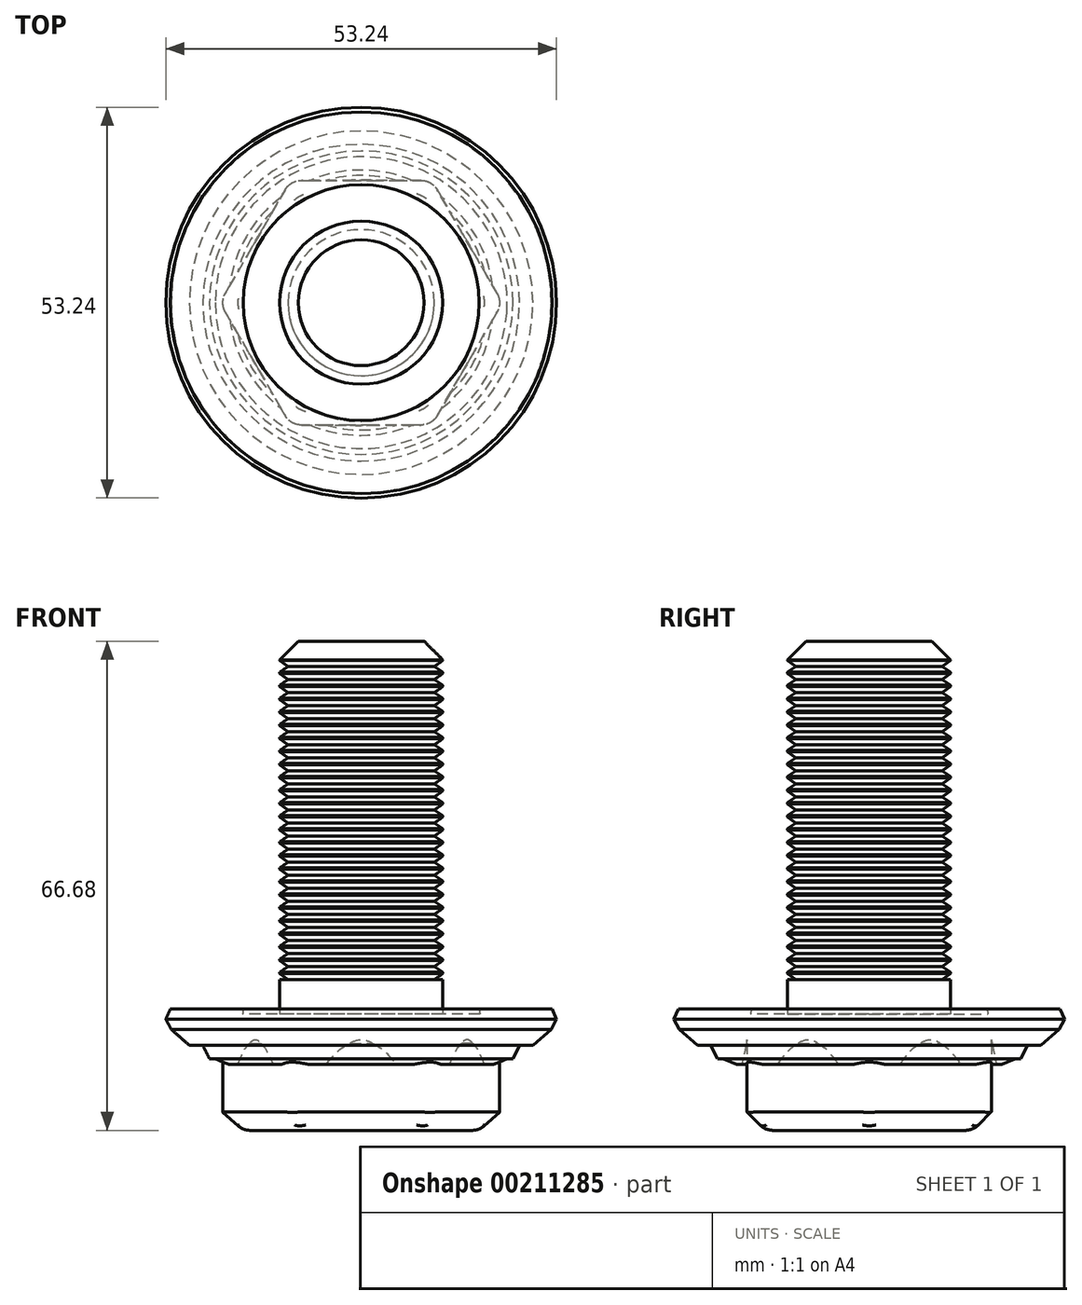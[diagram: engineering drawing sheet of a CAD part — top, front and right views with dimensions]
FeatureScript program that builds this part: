
annotation { "Feature Type Name" : "Feature", "Feature Type Description" : "" }
export const myFeature = defineFeature(function(context is Context, id is Id, definition is map)
    precondition{}
    {
        {
            var Q0;
            Q0=qCreatedBy(makeId("Top.planeOp"),FACE);
            var sketch = newSketch(context, id + "F0", { "sketchPlane" : qUnion([Q0])});
            skCircle(sketch, "E0.cCircle", {"center": v(0, 0) * mm, "radius": 16.67 * mm, "construction": true});
            skLineSegment(sketch, "E0.0", {"start": v(-9.62, 16.67) * mm, "end": v(9.62, 16.67) * mm});
            skLineSegment(sketch, "E0.1", {"start": v(9.62, 16.67) * mm, "end": v(19.25, 0) * mm});
            skLineSegment(sketch, "E0.2", {"start": v(19.25, 0) * mm, "end": v(9.62, -16.67) * mm});
            skLineSegment(sketch, "E0.3", {"start": v(9.62, -16.67) * mm, "end": v(-9.62, -16.67) * mm});
            skLineSegment(sketch, "E0.4", {"start": v(-9.62, -16.67) * mm, "end": v(-19.25, 0) * mm});
            skLineSegment(sketch, "E0.5", {"start": v(-19.25, 0) * mm, "end": v(-9.62, 16.67) * mm});
            skPoint(sketch, "E0.0.midPoint", {"position": v(0, 16.67) * mm});
            skSolve(sketch);
        }
        {
            var Q0;
            Q0=qSketchRegion(id+"F0",true);
            extrude(context, id + "F1", {"entities" : qUnion([Q0]), "depth" : 15.88 * mm});
        }
        {
            var Q0;
            Q0=makeQuery(id+"F1.opExtrude","CAP_FACE",FACE,{"disambiguationData":[OSD([sQuery(id+"F0.wireOp",EDGE,"E0.0"),sQuery(id+"F0.wireOp",EDGE,"E0.1"),sQuery(id+"F0.wireOp",EDGE,"E0.2"),sQuery(id+"F0.wireOp",EDGE,"E0.3"),sQuery(id+"F0.wireOp",EDGE,"E0.4"),sQuery(id+"F0.wireOp",EDGE,"E0.5")])],"isStart":false});
            var sketch = newSketch(context, id + "F2", { "sketchPlane" : qUnion([Q0])});
            skCircle(sketch, "E1", {"center": v(0, 0) * mm, "radius": 11.11 * mm});
            skSolve(sketch);
        }
        {
            var Q0;
            Q0=qSketchRegion(id+"F2",true);
            extrude(context, id + "F3", {"entities" : qUnion([Q0]), "operationType" : NewBodyOperationType.ADD, "depth" : 50.8 * mm});
        }
        {
            var Q0;
            Q0=makeQuery(id+"F3.opExtrude","CAP_EDGE",EDGE,{"disambiguationData":[OSD([sQuery(id+"F2.wireOp",EDGE,"E1")])],"isStart":false});
            var Q1;
            Q1=makeQuery(id+"F1.opExtrude","CAP_EDGE",EDGE,{"disambiguationData":[OSD([sQuery(id+"F0.wireOp",EDGE,"E0.5")])],"isStart":true});
            var Q2;
            Q2=makeQuery(id+"F1.opExtrude","CAP_EDGE",EDGE,{"disambiguationData":[OSD([sQuery(id+"F0.wireOp",EDGE,"E0.0")])],"isStart":true});
            var Q3;
            Q3=makeQuery(id+"F1.opExtrude","CAP_EDGE",EDGE,{"disambiguationData":[OSD([sQuery(id+"F0.wireOp",EDGE,"E0.1")])],"isStart":true});
            var Q4;
            Q4=makeQuery(id+"F1.opExtrude","CAP_EDGE",EDGE,{"disambiguationData":[OSD([sQuery(id+"F0.wireOp",EDGE,"E0.2")])],"isStart":true});
            var Q5;
            Q5=makeQuery(id+"F1.opExtrude","CAP_EDGE",EDGE,{"disambiguationData":[OSD([sQuery(id+"F0.wireOp",EDGE,"E0.3")])],"isStart":true});
            var Q6;
            Q6=makeQuery(id+"F1.opExtrude","CAP_EDGE",EDGE,{"disambiguationData":[OSD([sQuery(id+"F0.wireOp",EDGE,"E0.4")])],"isStart":true});
            chamfer(context, id + "F4", {"entities" : qUnion([Q0, Q1, Q2, Q3, Q4, Q5, Q6]), "width" : 2.54 * mm, "tangentPropagation" : true});
        }
        {
            var Q0;
            Q0=makeQuery(id+"F1.opExtrude","SWEPT_EDGE",EDGE,{"disambiguationData":[OSD([sQuery(id+"F0.wireOp",EDGE,"E0.0"),sQuery(id+"F0.wireOp",EDGE,"E0.5")])]});
            var Q1;
            Q1=makeQuery(id+"F1.opExtrude","SWEPT_EDGE",EDGE,{"disambiguationData":[OSD([sQuery(id+"F0.wireOp",EDGE,"E0.0"),sQuery(id+"F0.wireOp",EDGE,"E0.1")])]});
            var Q2;
            Q2=makeQuery(id+"F1.opExtrude","SWEPT_EDGE",EDGE,{"disambiguationData":[OSD([sQuery(id+"F0.wireOp",EDGE,"E0.1"),sQuery(id+"F0.wireOp",EDGE,"E0.2")])]});
            var Q3;
            Q3=makeQuery(id+"F1.opExtrude","SWEPT_EDGE",EDGE,{"disambiguationData":[OSD([sQuery(id+"F0.wireOp",EDGE,"E0.2"),sQuery(id+"F0.wireOp",EDGE,"E0.3")])]});
            var Q4;
            Q4=makeQuery(id+"F1.opExtrude","SWEPT_EDGE",EDGE,{"disambiguationData":[OSD([sQuery(id+"F0.wireOp",EDGE,"E0.3"),sQuery(id+"F0.wireOp",EDGE,"E0.4")])]});
            var Q5;
            Q5=makeQuery(id+"F1.opExtrude","SWEPT_EDGE",EDGE,{"disambiguationData":[OSD([sQuery(id+"F0.wireOp",EDGE,"E0.4"),sQuery(id+"F0.wireOp",EDGE,"E0.5")])]});
            var Q6;
            Q6=makeQuery(id+"F4.opChamfer","BLEND_EDGE",EDGE,{"blendedFrom":[makeQuery(id+"F1.opExtrude","CAP_EDGE",EDGE,{"disambiguationData":[OSD([sQuery(id+"F0.wireOp",EDGE,"E0.3")])],"isStart":true}),makeQuery(id+"F1.opExtrude","CAP_EDGE",EDGE,{"disambiguationData":[OSD([sQuery(id+"F0.wireOp",EDGE,"E0.4")])],"isStart":true})],"blendedInto":[]});
            var Q7;
            Q7=makeQuery(id+"F4.opChamfer","BLEND_EDGE",EDGE,{"blendedFrom":[makeQuery(id+"F1.opExtrude","CAP_EDGE",EDGE,{"disambiguationData":[OSD([sQuery(id+"F0.wireOp",EDGE,"E0.2")])],"isStart":true}),makeQuery(id+"F1.opExtrude","CAP_EDGE",EDGE,{"disambiguationData":[OSD([sQuery(id+"F0.wireOp",EDGE,"E0.3")])],"isStart":true})],"blendedInto":[]});
            var Q8;
            Q8=makeQuery(id+"F4.opChamfer","BLEND_EDGE",EDGE,{"blendedFrom":[makeQuery(id+"F1.opExtrude","CAP_EDGE",EDGE,{"disambiguationData":[OSD([sQuery(id+"F0.wireOp",EDGE,"E0.1")])],"isStart":true}),makeQuery(id+"F1.opExtrude","CAP_EDGE",EDGE,{"disambiguationData":[OSD([sQuery(id+"F0.wireOp",EDGE,"E0.2")])],"isStart":true})],"blendedInto":[]});
            var Q9;
            Q9=makeQuery(id+"F4.opChamfer","BLEND_EDGE",EDGE,{"blendedFrom":[makeQuery(id+"F1.opExtrude","CAP_EDGE",EDGE,{"disambiguationData":[OSD([sQuery(id+"F0.wireOp",EDGE,"E0.0")])],"isStart":true}),makeQuery(id+"F1.opExtrude","CAP_EDGE",EDGE,{"disambiguationData":[OSD([sQuery(id+"F0.wireOp",EDGE,"E0.1")])],"isStart":true})],"blendedInto":[]});
            var Q10;
            Q10=makeQuery(id+"F4.opChamfer","BLEND_EDGE",EDGE,{"blendedFrom":[makeQuery(id+"F1.opExtrude","CAP_EDGE",EDGE,{"disambiguationData":[OSD([sQuery(id+"F0.wireOp",EDGE,"E0.0")])],"isStart":true}),makeQuery(id+"F1.opExtrude","CAP_EDGE",EDGE,{"disambiguationData":[OSD([sQuery(id+"F0.wireOp",EDGE,"E0.5")])],"isStart":true})],"blendedInto":[]});
            var Q11;
            Q11=makeQuery(id+"F4.opChamfer","BLEND_EDGE",EDGE,{"blendedFrom":[makeQuery(id+"F1.opExtrude","CAP_EDGE",EDGE,{"disambiguationData":[OSD([sQuery(id+"F0.wireOp",EDGE,"E0.4")])],"isStart":true}),makeQuery(id+"F1.opExtrude","CAP_EDGE",EDGE,{"disambiguationData":[OSD([sQuery(id+"F0.wireOp",EDGE,"E0.5")])],"isStart":true})],"blendedInto":[]});
            var Q12;
            {var subQ0=sQuery(id+"F0.wireOp",EDGE,"E0.4");Q12=makeQuery(id+"F4.opChamfer","BLEND_EDGE",EDGE,{"blendedFrom":[makeQuery(id+"F1.opExtrude","CAP_EDGE",EDGE,{"disambiguationData":[OSD([subQ0])],"isStart":true}),makeQuery(id+"F1.opExtrude","CAP_FACE",FACE,{"disambiguationData":[OSD([sQuery(id+"F0.wireOp",EDGE,"E0.0"),sQuery(id+"F0.wireOp",EDGE,"E0.1"),sQuery(id+"F0.wireOp",EDGE,"E0.2"),sQuery(id+"F0.wireOp",EDGE,"E0.3"),subQ0,sQuery(id+"F0.wireOp",EDGE,"E0.5")])],"isStart":true})],"blendedInto":[makeQuery(id+"F1.opExtrude","CAP_FACE",FACE,{"disambiguationData":[OSD([sQuery(id+"F0.wireOp",EDGE,"E0.0"),sQuery(id+"F0.wireOp",EDGE,"E0.1"),sQuery(id+"F0.wireOp",EDGE,"E0.2"),sQuery(id+"F0.wireOp",EDGE,"E0.3"),subQ0,sQuery(id+"F0.wireOp",EDGE,"E0.5")])],"isStart":true})]});}
            var Q13;
            {var subQ0=sQuery(id+"F0.wireOp",EDGE,"E0.3");Q13=makeQuery(id+"F4.opChamfer","BLEND_EDGE",EDGE,{"blendedFrom":[makeQuery(id+"F1.opExtrude","CAP_EDGE",EDGE,{"disambiguationData":[OSD([subQ0])],"isStart":true}),makeQuery(id+"F1.opExtrude","CAP_FACE",FACE,{"disambiguationData":[OSD([sQuery(id+"F0.wireOp",EDGE,"E0.0"),sQuery(id+"F0.wireOp",EDGE,"E0.1"),sQuery(id+"F0.wireOp",EDGE,"E0.2"),subQ0,sQuery(id+"F0.wireOp",EDGE,"E0.4"),sQuery(id+"F0.wireOp",EDGE,"E0.5")])],"isStart":true})],"blendedInto":[makeQuery(id+"F1.opExtrude","CAP_FACE",FACE,{"disambiguationData":[OSD([sQuery(id+"F0.wireOp",EDGE,"E0.0"),sQuery(id+"F0.wireOp",EDGE,"E0.1"),sQuery(id+"F0.wireOp",EDGE,"E0.2"),subQ0,sQuery(id+"F0.wireOp",EDGE,"E0.4"),sQuery(id+"F0.wireOp",EDGE,"E0.5")])],"isStart":true})]});}
            var Q14;
            {var subQ0=sQuery(id+"F0.wireOp",EDGE,"E0.2");Q14=makeQuery(id+"F4.opChamfer","BLEND_EDGE",EDGE,{"blendedFrom":[makeQuery(id+"F1.opExtrude","CAP_EDGE",EDGE,{"disambiguationData":[OSD([subQ0])],"isStart":true}),makeQuery(id+"F1.opExtrude","CAP_FACE",FACE,{"disambiguationData":[OSD([sQuery(id+"F0.wireOp",EDGE,"E0.0"),sQuery(id+"F0.wireOp",EDGE,"E0.1"),subQ0,sQuery(id+"F0.wireOp",EDGE,"E0.3"),sQuery(id+"F0.wireOp",EDGE,"E0.4"),sQuery(id+"F0.wireOp",EDGE,"E0.5")])],"isStart":true})],"blendedInto":[makeQuery(id+"F1.opExtrude","CAP_FACE",FACE,{"disambiguationData":[OSD([sQuery(id+"F0.wireOp",EDGE,"E0.0"),sQuery(id+"F0.wireOp",EDGE,"E0.1"),subQ0,sQuery(id+"F0.wireOp",EDGE,"E0.3"),sQuery(id+"F0.wireOp",EDGE,"E0.4"),sQuery(id+"F0.wireOp",EDGE,"E0.5")])],"isStart":true})]});}
            var Q15;
            {var subQ0=sQuery(id+"F0.wireOp",EDGE,"E0.1");Q15=makeQuery(id+"F4.opChamfer","BLEND_EDGE",EDGE,{"blendedFrom":[makeQuery(id+"F1.opExtrude","CAP_EDGE",EDGE,{"disambiguationData":[OSD([subQ0])],"isStart":true}),makeQuery(id+"F1.opExtrude","CAP_FACE",FACE,{"disambiguationData":[OSD([sQuery(id+"F0.wireOp",EDGE,"E0.0"),subQ0,sQuery(id+"F0.wireOp",EDGE,"E0.2"),sQuery(id+"F0.wireOp",EDGE,"E0.3"),sQuery(id+"F0.wireOp",EDGE,"E0.4"),sQuery(id+"F0.wireOp",EDGE,"E0.5")])],"isStart":true})],"blendedInto":[makeQuery(id+"F1.opExtrude","CAP_FACE",FACE,{"disambiguationData":[OSD([sQuery(id+"F0.wireOp",EDGE,"E0.0"),subQ0,sQuery(id+"F0.wireOp",EDGE,"E0.2"),sQuery(id+"F0.wireOp",EDGE,"E0.3"),sQuery(id+"F0.wireOp",EDGE,"E0.4"),sQuery(id+"F0.wireOp",EDGE,"E0.5")])],"isStart":true})]});}
            var Q16;
            {var subQ0=sQuery(id+"F0.wireOp",EDGE,"E0.0");Q16=makeQuery(id+"F4.opChamfer","BLEND_EDGE",EDGE,{"blendedFrom":[makeQuery(id+"F1.opExtrude","CAP_EDGE",EDGE,{"disambiguationData":[OSD([subQ0])],"isStart":true}),makeQuery(id+"F1.opExtrude","CAP_FACE",FACE,{"disambiguationData":[OSD([subQ0,sQuery(id+"F0.wireOp",EDGE,"E0.1"),sQuery(id+"F0.wireOp",EDGE,"E0.2"),sQuery(id+"F0.wireOp",EDGE,"E0.3"),sQuery(id+"F0.wireOp",EDGE,"E0.4"),sQuery(id+"F0.wireOp",EDGE,"E0.5")])],"isStart":true})],"blendedInto":[makeQuery(id+"F1.opExtrude","CAP_FACE",FACE,{"disambiguationData":[OSD([subQ0,sQuery(id+"F0.wireOp",EDGE,"E0.1"),sQuery(id+"F0.wireOp",EDGE,"E0.2"),sQuery(id+"F0.wireOp",EDGE,"E0.3"),sQuery(id+"F0.wireOp",EDGE,"E0.4"),sQuery(id+"F0.wireOp",EDGE,"E0.5")])],"isStart":true})]});}
            var Q17;
            {var subQ0=sQuery(id+"F0.wireOp",EDGE,"E0.5");Q17=makeQuery(id+"F4.opChamfer","BLEND_EDGE",EDGE,{"blendedFrom":[makeQuery(id+"F1.opExtrude","CAP_EDGE",EDGE,{"disambiguationData":[OSD([subQ0])],"isStart":true}),makeQuery(id+"F1.opExtrude","CAP_FACE",FACE,{"disambiguationData":[OSD([sQuery(id+"F0.wireOp",EDGE,"E0.0"),sQuery(id+"F0.wireOp",EDGE,"E0.1"),sQuery(id+"F0.wireOp",EDGE,"E0.2"),sQuery(id+"F0.wireOp",EDGE,"E0.3"),sQuery(id+"F0.wireOp",EDGE,"E0.4"),subQ0])],"isStart":true})],"blendedInto":[makeQuery(id+"F1.opExtrude","CAP_FACE",FACE,{"disambiguationData":[OSD([sQuery(id+"F0.wireOp",EDGE,"E0.0"),sQuery(id+"F0.wireOp",EDGE,"E0.1"),sQuery(id+"F0.wireOp",EDGE,"E0.2"),sQuery(id+"F0.wireOp",EDGE,"E0.3"),sQuery(id+"F0.wireOp",EDGE,"E0.4"),subQ0])],"isStart":true})]});}
            fillet(context, id + "F5", {"entities" : qUnion([Q0, Q1, Q2, Q3, Q4, Q5, Q6, Q7, Q8, Q9, Q10, Q11, Q12, Q13, Q14, Q15, Q16, Q17]), "radius" : 2.54 * mm, "tangentPropagation" : true, "allowEdgeOverflow" : false});
        }
        {
            var Q0;
            Q0=qCreatedBy(makeId("Front.planeOp"),FACE);
            var sketch = newSketch(context, id + "F6", { "sketchPlane" : qUnion([Q0])});
            skLineSegment(sketch, "E2", {"start": v(0, 0) * mm, "end": v(0, 73.73) * mm});
            skLineSegment(sketch, "E3", {"start": v(-1.25, 58.78) * mm, "end": v(-1.25, 57) * mm});
            skLineSegment(sketch, "E4", {"start": v(11.24, 64.12) * mm, "end": v(9.97, 63.23) * mm});
            skLineSegment(sketch, "E5", {"start": v(9.97, 63.23) * mm, "end": v(11.24, 62.34) * mm});
            skLineSegment(sketch, "E6", {"start": v(11.24, 62.34) * mm, "end": v(9.97, 61.45) * mm});
            skLineSegment(sketch, "E7", {"start": v(9.97, 61.45) * mm, "end": v(11.24, 60.56) * mm});
            skLineSegment(sketch, "E8", {"start": v(11.24, 60.56) * mm, "end": v(9.97, 59.67) * mm});
            skLineSegment(sketch, "E9", {"start": v(9.97, 59.67) * mm, "end": v(11.24, 58.78) * mm});
            skLineSegment(sketch, "E10", {"start": v(11.24, 58.78) * mm, "end": v(9.97, 57.9) * mm});
            skLineSegment(sketch, "E11", {"start": v(9.97, 57.9) * mm, "end": v(11.24, 57) * mm});
            skLineSegment(sketch, "E12", {"start": v(11.24, 57) * mm, "end": v(9.97, 56.12) * mm});
            skLineSegment(sketch, "E13.0.1.0", {"start": v(9.97, 56.12) * mm, "end": v(11.24, 55.23) * mm});
            skLineSegment(sketch, "E13.0.1.1", {"start": v(11.24, 55.23) * mm, "end": v(9.97, 54.34) * mm});
            skLineSegment(sketch, "E13.0.1.2", {"start": v(9.97, 54.34) * mm, "end": v(11.24, 53.45) * mm});
            skLineSegment(sketch, "E13.0.1.4", {"start": v(11.24, 53.45) * mm, "end": v(9.97, 52.56) * mm});
            skLineSegment(sketch, "E13.0.1.5", {"start": v(9.97, 50.78) * mm, "end": v(11.24, 49.9) * mm});
            skLineSegment(sketch, "E13.0.1.6", {"start": v(11.24, 51.67) * mm, "end": v(9.97, 50.78) * mm});
            skLineSegment(sketch, "E13.0.1.7", {"start": v(11.24, 49.9) * mm, "end": v(9.97, 49) * mm});
            skLineSegment(sketch, "E13.0.1.8", {"start": v(9.97, 52.56) * mm, "end": v(11.24, 51.67) * mm});
            skLineSegment(sketch, "E13.0.2.0", {"start": v(9.97, 49) * mm, "end": v(11.24, 48.12) * mm});
            skLineSegment(sketch, "E13.0.2.1", {"start": v(11.24, 48.12) * mm, "end": v(9.97, 47.23) * mm});
            skLineSegment(sketch, "E13.0.2.2", {"start": v(9.97, 47.23) * mm, "end": v(11.24, 46.34) * mm});
            skLineSegment(sketch, "E13.0.2.3", {"start": v(11.24, 49.9) * mm, "end": v(9.97, 49) * mm});
            skLineSegment(sketch, "E13.0.2.4", {"start": v(11.24, 46.34) * mm, "end": v(9.97, 45.45) * mm});
            skLineSegment(sketch, "E13.0.2.5", {"start": v(9.97, 43.67) * mm, "end": v(11.24, 42.78) * mm});
            skLineSegment(sketch, "E13.0.2.6", {"start": v(11.24, 44.56) * mm, "end": v(9.97, 43.67) * mm});
            skLineSegment(sketch, "E13.0.2.7", {"start": v(11.24, 42.78) * mm, "end": v(9.97, 41.9) * mm});
            skLineSegment(sketch, "E13.0.2.8", {"start": v(9.97, 45.45) * mm, "end": v(11.24, 44.56) * mm});
            skLineSegment(sketch, "E13.0.3.0", {"start": v(9.97, 41.9) * mm, "end": v(11.24, 41) * mm});
            skLineSegment(sketch, "E13.0.3.1", {"start": v(11.24, 41) * mm, "end": v(9.97, 40.11) * mm});
            skLineSegment(sketch, "E13.0.3.2", {"start": v(9.97, 40.11) * mm, "end": v(11.24, 39.23) * mm});
            skLineSegment(sketch, "E13.0.3.3", {"start": v(11.24, 42.78) * mm, "end": v(9.97, 41.9) * mm});
            skLineSegment(sketch, "E13.0.3.4", {"start": v(11.24, 39.23) * mm, "end": v(9.97, 38.34) * mm});
            skLineSegment(sketch, "E13.0.3.5", {"start": v(9.97, 36.56) * mm, "end": v(11.24, 35.67) * mm});
            skLineSegment(sketch, "E13.0.3.6", {"start": v(11.24, 37.45) * mm, "end": v(9.97, 36.56) * mm});
            skLineSegment(sketch, "E13.0.3.7", {"start": v(11.24, 35.67) * mm, "end": v(9.97, 34.78) * mm});
            skLineSegment(sketch, "E13.0.3.8", {"start": v(9.97, 38.34) * mm, "end": v(11.24, 37.45) * mm});
            skLineSegment(sketch, "E13.0.4.0", {"start": v(9.97, 34.78) * mm, "end": v(11.24, 33.9) * mm});
            skLineSegment(sketch, "E13.0.4.1", {"start": v(11.24, 33.9) * mm, "end": v(9.97, 33) * mm});
            skLineSegment(sketch, "E13.0.4.2", {"start": v(9.97, 33) * mm, "end": v(11.24, 32.11) * mm});
            skLineSegment(sketch, "E13.0.4.3", {"start": v(11.24, 35.67) * mm, "end": v(9.97, 34.78) * mm});
            skLineSegment(sketch, "E13.0.4.4", {"start": v(11.24, 32.11) * mm, "end": v(9.97, 31.22) * mm});
            skLineSegment(sketch, "E13.0.4.5", {"start": v(9.97, 29.45) * mm, "end": v(11.24, 28.56) * mm});
            skLineSegment(sketch, "E13.0.4.6", {"start": v(11.24, 30.34) * mm, "end": v(9.97, 29.45) * mm});
            skLineSegment(sketch, "E13.0.4.7", {"start": v(11.24, 28.56) * mm, "end": v(9.97, 27.67) * mm});
            skLineSegment(sketch, "E13.0.4.8", {"start": v(9.97, 31.22) * mm, "end": v(11.24, 30.34) * mm});
            skLineSegment(sketch, "E13.0.5.0", {"start": v(9.97, 27.67) * mm, "end": v(11.24, 26.78) * mm});
            skLineSegment(sketch, "E13.0.5.1", {"start": v(11.24, 26.78) * mm, "end": v(9.97, 25.9) * mm});
            skLineSegment(sketch, "E13.0.5.2", {"start": v(9.97, 25.9) * mm, "end": v(11.24, 25) * mm});
            skLineSegment(sketch, "E13.0.5.3", {"start": v(11.24, 28.56) * mm, "end": v(9.97, 27.67) * mm});
            skLineSegment(sketch, "E13.0.5.4", {"start": v(11.24, 25) * mm, "end": v(9.97, 24.11) * mm});
            skLineSegment(sketch, "E13.0.5.5", {"start": v(9.97, 22.33) * mm, "end": v(11.24, 21.45) * mm});
            skLineSegment(sketch, "E13.0.5.6", {"start": v(11.24, 23.22) * mm, "end": v(9.97, 22.33) * mm});
            skLineSegment(sketch, "E13.0.5.7", {"start": v(11.24, 21.45) * mm, "end": v(9.97, 20.56) * mm});
            skLineSegment(sketch, "E13.0.5.8", {"start": v(9.97, 24.11) * mm, "end": v(11.24, 23.22) * mm});
            skLineSegment(sketch, "E14", {"start": v(9.97, 20.56) * mm, "end": v(11.95, 20.56) * mm});
            skLineSegment(sketch, "E15", {"start": v(11.95, 20.56) * mm, "end": v(11.95, 65) * mm});
            skLineSegment(sketch, "E16", {"start": v(11.95, 65) * mm, "end": v(11.24, 64.12) * mm});
            skSolve(sketch);
        }
        {
            var Q0;
            Q0 = qSketchRegion(id + "F6", true);
            var Q1;
            Q1=sQuery(id+"F6.wireOp",EDGE,"E2");
            revolve(context, id + "F7", {"operationType" : NewBodyOperationType.REMOVE, "entities" : qUnion([Q0]), "axis" : qUnion([Q1]), "revolveType" : RevolveType.FULL, "oppositeDirection" : true});
        }
        {
            var Q0;
            Q0=qCreatedBy(makeId("Front.planeOp"),FACE);
            var sketch = newSketch(context, id + "F8", { "sketchPlane" : qUnion([Q0])});
            skLineSegment(sketch, "E17", {"start": v(16.07, 16.55) * mm, "end": v(26.02, 16.55) * mm});
            skLineSegment(sketch, "E18", {"start": v(26.02, 16.55) * mm, "end": v(26.62, 15.15) * mm});
            skLineSegment(sketch, "E19", {"start": v(26.62, 15.15) * mm, "end": v(25.9, 13.76) * mm});
            skLineSegment(sketch, "E20", {"start": v(25.9, 13.76) * mm, "end": v(23.4, 11.58) * mm});
            skLineSegment(sketch, "E21", {"start": v(23.4, 11.58) * mm, "end": v(21.59, 11.58) * mm});
            skLineSegment(sketch, "E22", {"start": v(21.59, 11.58) * mm, "end": v(20.68, 9.76) * mm});
            skLineSegment(sketch, "E23", {"start": v(20.68, 9.76) * mm, "end": v(19.9, 9.76) * mm});
            skLineSegment(sketch, "E24", {"start": v(19.9, 9.76) * mm, "end": v(18.07, 8.97) * mm});
            skLineSegment(sketch, "E25", {"start": v(18.07, 8.97) * mm, "end": v(17.34, 8.97) * mm});
            skLineSegment(sketch, "E26", {"start": v(17.34, 8.97) * mm, "end": v(16.74, 11.88) * mm});
            skLineSegment(sketch, "E27", {"start": v(16.74, 11.88) * mm, "end": v(16.07, 16.55) * mm});
            skLineSegment(sketch, "E28", {"start": v(0, -10.94) * mm, "end": v(0, 78.01) * mm});
            skSolve(sketch);
        }
        {
            var Q0;
            Q0 = qSketchRegion(id + "F8", true);
            var Q1;
            Q1=sQuery(id+"F8.wireOp",EDGE,"E28");
            revolve(context, id + "F9", {"operationType" : NewBodyOperationType.ADD, "entities" : qUnion([Q0]), "axis" : qUnion([Q1]), "revolveType" : RevolveType.FULL});
        }
    });
